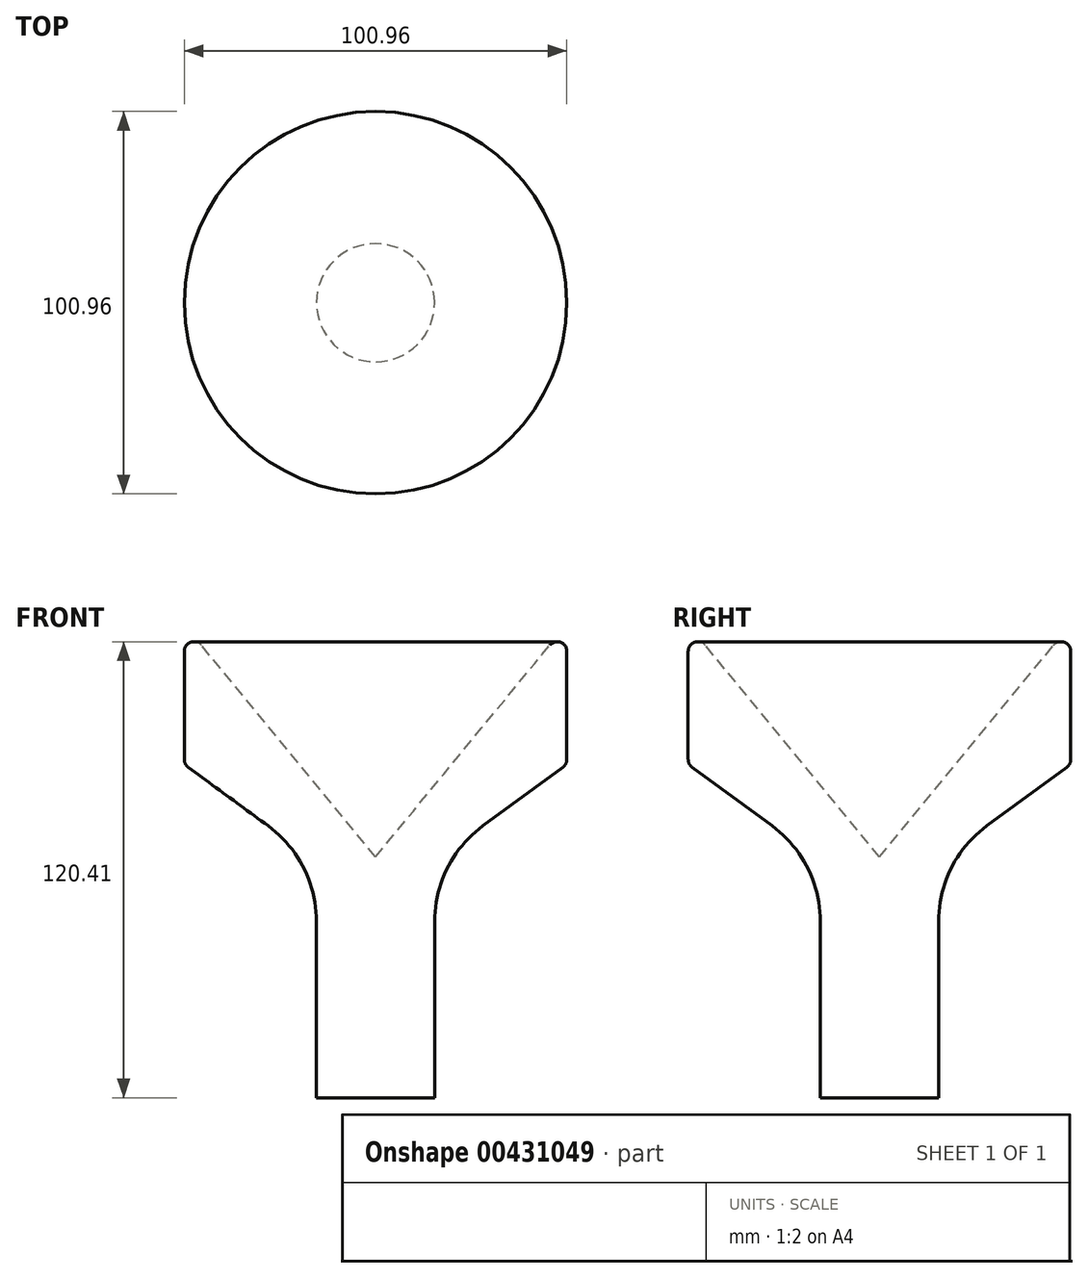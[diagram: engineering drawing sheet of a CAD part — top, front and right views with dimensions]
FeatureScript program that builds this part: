
annotation { "Feature Type Name" : "Feature", "Feature Type Description" : "" }
export const myFeature = defineFeature(function(context is Context, id is Id, definition is map)
    precondition{}
    {
        {
            var Q0;
            Q0=qCreatedBy(makeId("Front.planeOp"),FACE);
            var sketch = newSketch(context, id + "F0", { "sketchPlane" : qUnion([Q0])});
            skLineSegment(sketch, "E0", {"start": v(0, 0) * mm, "end": v(0, 44.1) * mm, "construction": true});
            skLineSegment(sketch, "E1", {"start": v(0, 0) * mm, "end": v(50.48, 61.42) * mm});
            skLineSegment(sketch, "E2", {"start": v(50.48, 61.42) * mm, "end": v(50.48, 24.47) * mm});
            skLineSegment(sketch, "E3", {"start": v(50.48, 24.47) * mm, "end": v(28.36, 8.24) * mm});
            skArc(sketch, "E4", {"start": v(28.36, 8.24) * mm, "mid": v(18.97, -2.84) * mm, "end": v(15.6, -16.96) * mm});
            skLineSegment(sketch, "E5", {"start": v(15.6, -16.96) * mm, "end": v(15.6, -63.54) * mm});
            skLineSegment(sketch, "E6", {"start": v(15.6, -63.54) * mm, "end": v(0, -63.54) * mm});
            skLineSegment(sketch, "E7", {"start": v(0, 0) * mm, "end": v(0, -63.54) * mm});
            skSolve(sketch);
        }
        {
            var Q0;
            Q0=makeQuery(id+"F0.imprint","IMPRINT",FACE,{"disambiguationData":[TD([[makeQuery(id+"F0.imprint","IMPRINT",EDGE,{"derivedFrom":sQuery(id+"F0.wireOp",EDGE,"E0")}),-1.0]])]});
            var Q1;
            Q1=makeQuery(id+"F0.imprint","IMPRINT",FACE,{"disambiguationData":[TD([[makeQuery(id+"F0.imprint","IMPRINT",EDGE,{"derivedFrom":sQuery(id+"F0.wireOp",EDGE,"E1")}),-1.0]])]});
            var Q2;
            Q2=sQuery(id+"F0.wireOp",EDGE,"E0");
            revolve(context, id + "F1", {"entities" : qUnion([Q0, Q1]), "axis" : qUnion([Q2]), "revolveType" : RevolveType.FULL});
        }
        {
            var Q0;
            Q0=makeQuery(id+"F1.opRevolve","SWEPT_EDGE",EDGE,{"disambiguationData":[OSD([sQuery(id+"F0.wireOp",EDGE,"E1"),sQuery(id+"F0.wireOp",EDGE,"E2")])]});
            var Q1;
            Q1=makeQuery(id+"F1.opRevolve","SWEPT_EDGE",EDGE,{"disambiguationData":[OSD([sQuery(id+"F0.wireOp",EDGE,"E2"),sQuery(id+"F0.wireOp",EDGE,"E3")])]});
            fillet(context, id + "F2", {"entities" : qUnion([Q0, Q1]), "radius" : 2.54 * mm, "tangentPropagation" : true, "allowEdgeOverflow" : false});
        }
    });
